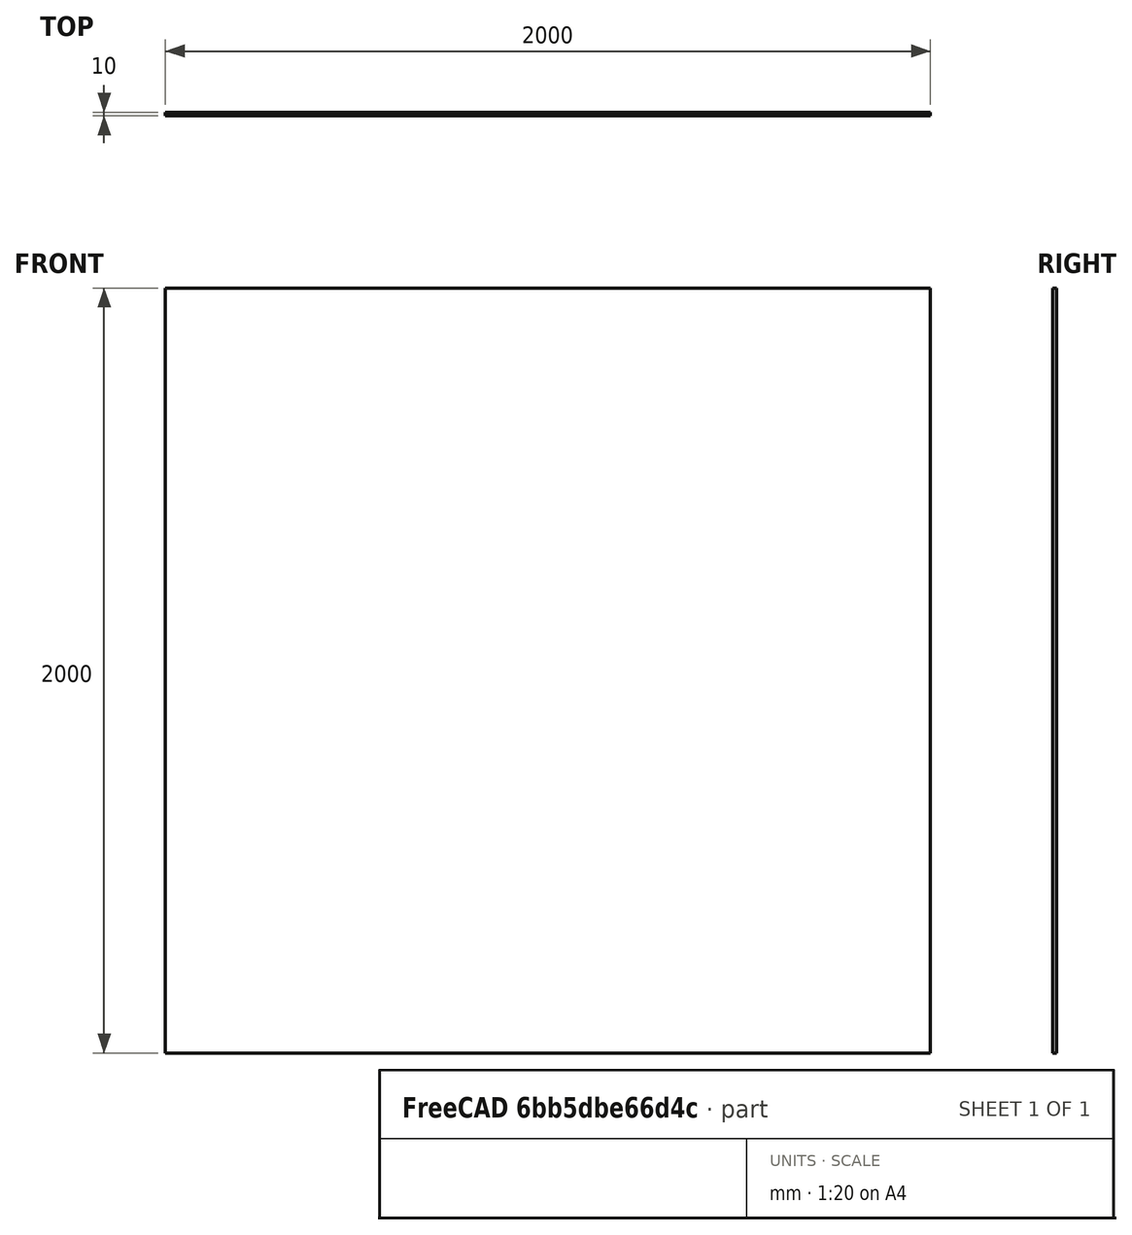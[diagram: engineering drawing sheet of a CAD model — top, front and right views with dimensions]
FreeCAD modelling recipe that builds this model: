
FCSTD DOCUMENT  (FreeCAD 1.0R39319 (Git))
Label: Floor
License: All rights reserved
LicenseURL: https://en.wikipedia.org/wiki/All_rights_reserved
objects: PartDesign::CoordinateSystem×3, Sketcher::SketchObject×1, PartDesign::Pad×1, PartDesign::Body×1, App::Part×1
note: 9 computed .brp shape members not serialized (recipe doc carries the construction recipe); baked Part::Feature solids carry a one-line shape summary decoded from their .brp

FEATURE [Sketcher::SketchObject] Sketch
  ArcFitTolerance = 1e-06
  AttachmentSupport = -> [XZ_Plane001]
  FullyConstrained = false
  MakeInternals = false
  MapMode = 5
  Placement = pos=(0,0,0) rot=(1,0,0;1.5708rad)
  sketch-geometry (4):
    g0: LineSegment StartX=-999.904 StartY=500 StartZ=0 EndX=-1000.1 EndY=-1500 EndZ=0
    g1: LineSegment StartX=-1000.1 StartY=-1500 StartZ=0 EndX=999.904 EndY=-1500 EndZ=0
    g2: LineSegment StartX=999.904 StartY=-1500 StartZ=0 EndX=999.904 EndY=500 EndZ=0
    g3: LineSegment StartX=999.904 StartY=500 StartZ=0 EndX=-999.904 EndY=500 EndZ=0
  constraints (10):
    c: Coincident(g0,g1)
    c: Coincident(g1,g2)
    c: Coincident(g2,g3)
    c: Coincident(g3,g0)
    c: Vertical(g2)
    c: Horizontal(g1)
    c: Distance(g2,g0) = 2000
    c: Distance(g1,g3) = 2000
    c: Symmetric(g0,g2,g-2)
    c: Distance(g3,g-1) = 500
FEATURE [PartDesign::Pad] Pad
  Direction = (0,-1,2e-16)
  Length = 10
  Length2 = 10
  Placement = pos=(0,0,0) rot=(1,0,0;1.5708rad)
  Profile = -> Sketch
  ReferenceAxis = -> Sketch [N_Axis]
  Refine = true
  Suppressed = false
  Type = 0
FEATURE [PartDesign::Body] Body  label="Floor001"
  AllowCompound = false
  Group = -> [Sketch,Pad]
  Origin = -> Origin001
  Tip = -> Pad
FEATURE [PartDesign::CoordinateSystem] reference_point  label="reference point"
  AttacherType = Attacher::AttachEngine3D
FEATURE [PartDesign::CoordinateSystem] ball_flight  label="ball flight"
  AttacherType = Attacher::AttachEngine3D
  AttachmentOffset = pos=(0,177.25,-422.25) rot=(0,0,1;0rad)
  AttachmentSupport = -> [XY_Plane]
  MapMode = 5
  Placement = pos=(0,177.25,-422.25) rot=(0,0,1;0rad)
FEATURE [PartDesign::CoordinateSystem] ball_tee_back  label="ball tee back"
  AttacherType = Attacher::AttachEngine3D
  AttachmentOffset = pos=(-522.75,0,-431.25) rot=(0,0,1;0rad)
  AttachmentSupport = -> [XY_Plane]
  MapMode = 5
  Placement = pos=(-522.75,0,-431.25) rot=(0,0,1;0rad)
FEATURE [App::Part] Part  label="Floor"
  Group = -> [Body,reference_point,ball_flight,ball_tee_back]
  Origin = -> Origin
